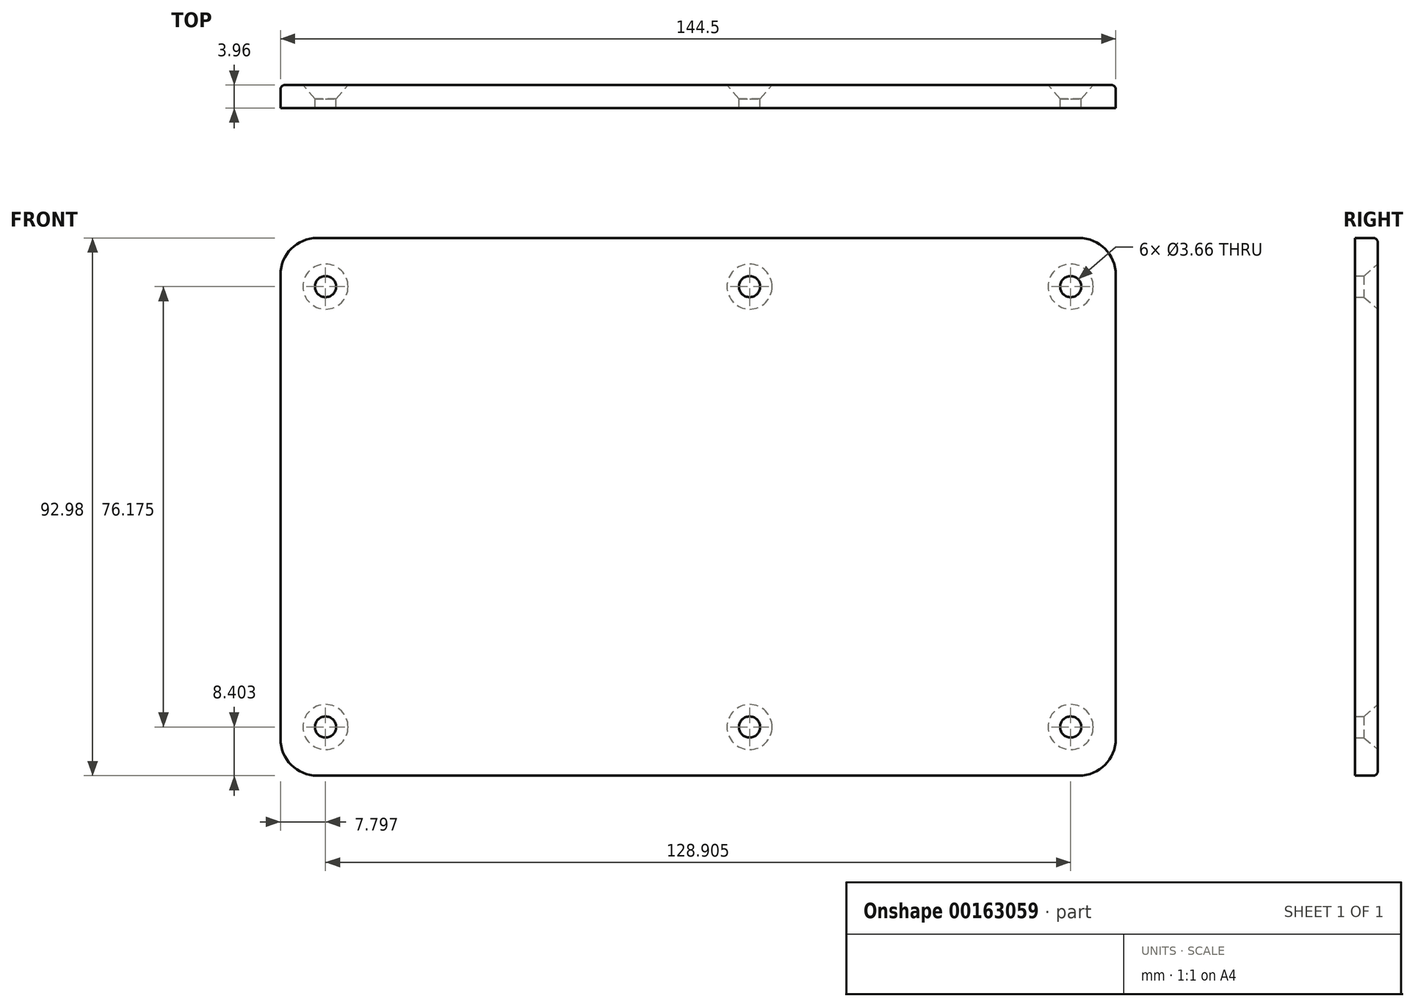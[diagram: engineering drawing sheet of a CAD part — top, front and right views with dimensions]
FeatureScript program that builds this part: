
annotation { "Feature Type Name" : "Feature", "Feature Type Description" : "" }
export const myFeature = defineFeature(function(context is Context, id is Id, definition is map)
    precondition{}
    {
        {
            var Q0;
            Q0=qCreatedBy(makeId("Front.planeOp"),FACE);
            var sketch = newSketch(context, id + "F0", { "sketchPlane" : qUnion([Q0])});
            skLineSegment(sketch, "E0.bottom", {"start": v(-72.25, -46.5) * mm, "end": v(72.25, -46.5) * mm});
            skLineSegment(sketch, "E0.top", {"start": v(-72.25, 46.5) * mm, "end": v(72.25, 46.5) * mm});
            skLineSegment(sketch, "E0.left", {"start": v(-72.25, -46.5) * mm, "end": v(-72.25, 46.5) * mm});
            skLineSegment(sketch, "E0.right", {"start": v(72.25, -46.5) * mm, "end": v(72.25, 46.5) * mm});
            skPoint(sketch, "E0.middle", {"position": v(0, 0) * mm});
            skSolve(sketch);
        }
        {
            var Q0;
            Q0=qSketchRegion(id+"F0",true);
            extrude(context, id + "F1", {"entities" : qUnion([Q0]), "oppositeDirection" : true, "depth" : 3.96 * mm});
        }
        {
            var Q0;
            Q0=makeQuery(id+"F1.opExtrude","CAP_FACE",FACE,{"disambiguationData":[OSD([sQuery(id+"F0.wireOp",EDGE,"E0.bottom"),sQuery(id+"F0.wireOp",EDGE,"E0.top"),sQuery(id+"F0.wireOp",EDGE,"E0.left"),sQuery(id+"F0.wireOp",EDGE,"E0.right")])],"isStart":false});
            var sketch = newSketch(context, id + "F2", { "sketchPlane" : qUnion([Q0])});
            skPoint(sketch, "E1", {"position": v(-64.45, 38.09) * mm});
            skPoint(sketch, "E2", {"position": v(-64.45, -38.09) * mm});
            skPoint(sketch, "E3", {"position": v(-8.9, 38.09) * mm});
            skPoint(sketch, "E4", {"position": v(64.45, 38.09) * mm});
            skPoint(sketch, "E5", {"position": v(64.45, -38.09) * mm});
            skPoint(sketch, "E6", {"position": v(-8.9, -38.09) * mm});
            skSolve(sketch);
        }
        {
            var Q0;
            Q0=sQuery(id+"F2.wireOp",VERTEX,"E1");
            var Q1;
            Q1=sQuery(id+"F2.wireOp",VERTEX,"E3");
            var Q2;
            Q2=sQuery(id+"F2.wireOp",VERTEX,"E4");
            var Q3;
            Q3=sQuery(id+"F2.wireOp",VERTEX,"E5");
            var Q4;
            Q4=sQuery(id+"F2.wireOp",VERTEX,"E6");
            var Q5;
            Q5=sQuery(id+"F2.wireOp",VERTEX,"E2");
            var Q6;
            Q6=makeQuery(id+"F1.opExtrude","SWEPT_BODY",BODY,{"disambiguationData":[OSD([sQuery(id+"F0.wireOp",EDGE,"E0.bottom"),sQuery(id+"F0.wireOp",EDGE,"E0.top"),sQuery(id+"F0.wireOp",EDGE,"E0.left"),sQuery(id+"F0.wireOp",EDGE,"E0.right")])]});
            hole(context, id + "F3", {"style" : HoleStyle.C_SINK, "endStyle" : HoleEndStyle.THROUGH, "standardTappedOrClearance" : lookupTablePath({ "standard" : "ANSI", "fit" : "Close", "size" : "#6", "type" : "Clearance" }), "standardBlindInLast" : lookupTablePath({ "fit" : "Close", "standard" : "ANSI", "size" : "#6", "type" : "Clearance" }), "holeDiameter" : 3.66 * mm, "cSinkDiameter" : 7.8 * mm, "cSinkAngle" : 82 * degree, "startFromSketch" : true, "locations" : qUnion([Q0, Q1, Q2, Q3, Q4, Q5]), "scope" : qUnion([Q6]), "isTappedThrough" : true});
        }
        {
            var Q0;
            Q0=makeQuery(id+"F1.opExtrude","SWEPT_EDGE",EDGE,{"disambiguationData":[OSD([sQuery(id+"F0.wireOp",EDGE,"E0.top"),sQuery(id+"F0.wireOp",EDGE,"E0.right")])]});
            var Q1;
            Q1=makeQuery(id+"F1.opExtrude","SWEPT_EDGE",EDGE,{"disambiguationData":[OSD([sQuery(id+"F0.wireOp",EDGE,"E0.bottom"),sQuery(id+"F0.wireOp",EDGE,"E0.right")])]});
            var Q2;
            Q2=makeQuery(id+"F1.opExtrude","SWEPT_EDGE",EDGE,{"disambiguationData":[OSD([sQuery(id+"F0.wireOp",EDGE,"E0.bottom"),sQuery(id+"F0.wireOp",EDGE,"E0.left")])]});
            var Q3;
            Q3=makeQuery(id+"F1.opExtrude","SWEPT_EDGE",EDGE,{"disambiguationData":[OSD([sQuery(id+"F0.wireOp",EDGE,"E0.top"),sQuery(id+"F0.wireOp",EDGE,"E0.left")])]});
            fillet(context, id + "F4", {"entities" : qUnion([Q0, Q1, Q2, Q3]), "radius" : 6.35 * mm, "tangentPropagation" : true, "allowEdgeOverflow" : false});
        }
        {
            var Q0;
            Q0=makeQuery(id+"F1.opExtrude","CAP_EDGE",EDGE,{"disambiguationData":[OSD([sQuery(id+"F0.wireOp",EDGE,"E0.bottom")])],"isStart":false});
            fillet(context, id + "F5", {"entities" : qUnion([Q0]), "radius" : 0.76 * mm, "tangentPropagation" : true, "allowEdgeOverflow" : false});
        }
    });
